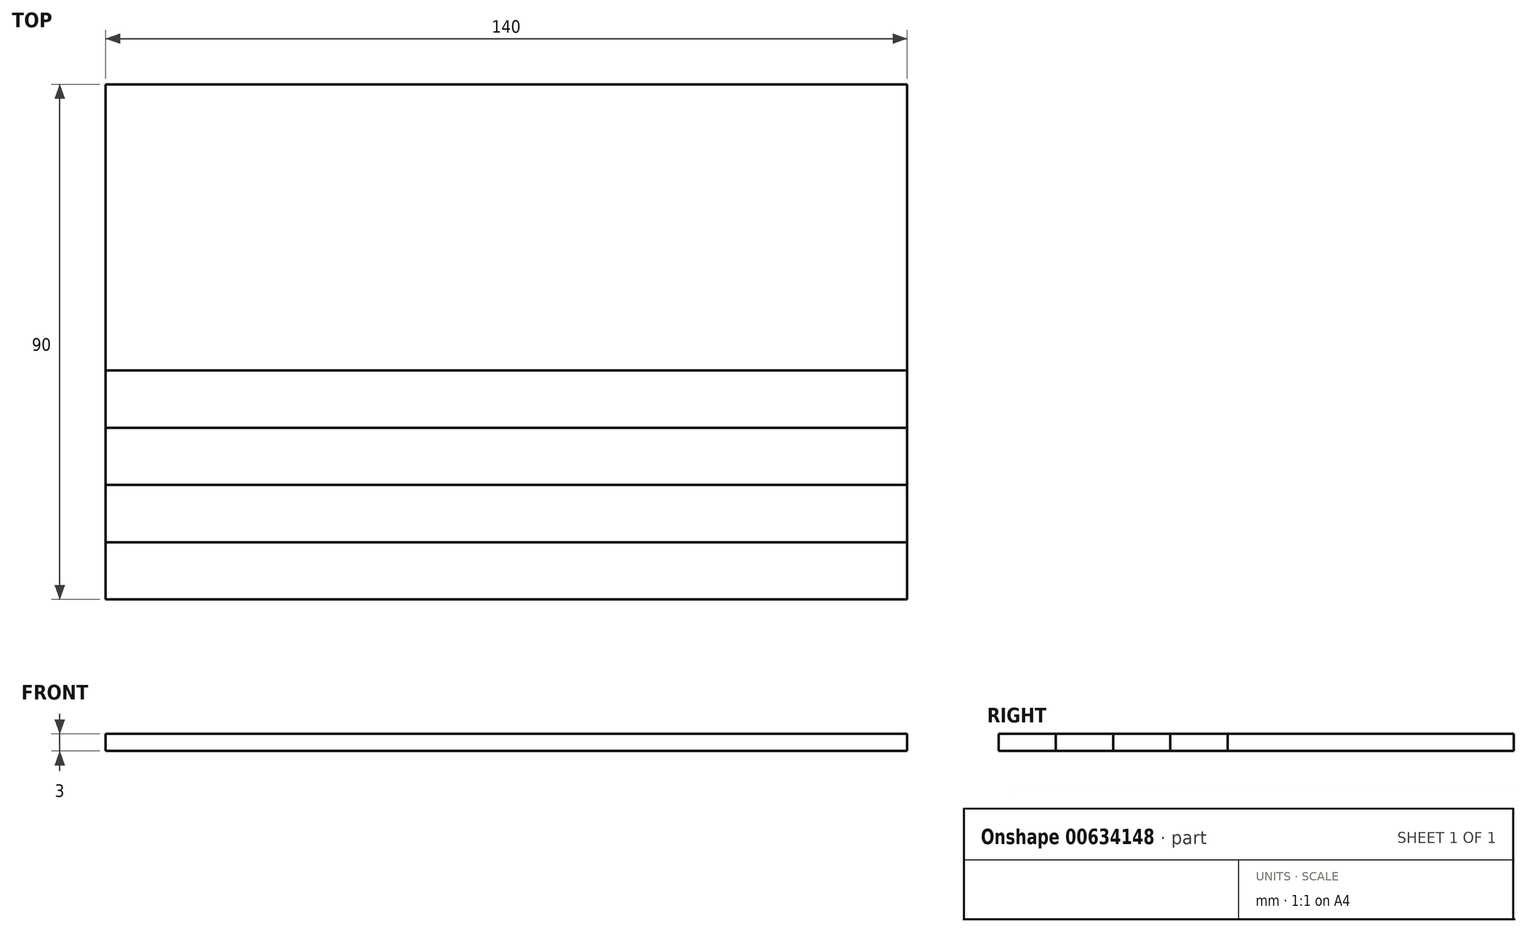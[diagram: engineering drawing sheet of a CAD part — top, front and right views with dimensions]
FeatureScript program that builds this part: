
annotation { "Feature Type Name" : "Feature", "Feature Type Description" : "" }
export const myFeature = defineFeature(function(context is Context, id is Id, definition is map)
    precondition{}
    {
        {
            var Q0;
            Q0=qCreatedBy(makeId("Right.planeOp"),FACE);
            var sketch = newSketch(context, id + "F0", { "sketchPlane" : qUnion([Q0])});
            skLineSegment(sketch, "E0.bottom", {"start": v(-10, 3) * mm, "end": v(0, 3) * mm});
            skLineSegment(sketch, "E0.top", {"start": v(-10, 0) * mm, "end": v(0, 0) * mm});
            skLineSegment(sketch, "E0.left", {"start": v(-10, 3) * mm, "end": v(-10, 0) * mm});
            skLineSegment(sketch, "E0.right", {"start": v(0, 3) * mm, "end": v(0, 0) * mm});
            skLineSegment(sketch, "E1.1.0.0", {"start": v(0, 0) * mm, "end": v(10, 0) * mm});
            skLineSegment(sketch, "E1.1.0.1", {"start": v(0, 3) * mm, "end": v(10, 3) * mm});
            skLineSegment(sketch, "E1.1.0.2", {"start": v(10, 3) * mm, "end": v(10, 0) * mm});
            skLineSegment(sketch, "E1.2.0.0", {"start": v(10, 0) * mm, "end": v(20, 0) * mm});
            skLineSegment(sketch, "E1.2.0.1", {"start": v(10, 3) * mm, "end": v(20, 3) * mm});
            skLineSegment(sketch, "E1.2.0.2", {"start": v(20, 3) * mm, "end": v(20, 0) * mm});
            skLineSegment(sketch, "E1.2.0.3", {"start": v(10, 3) * mm, "end": v(10, 0) * mm});
            skLineSegment(sketch, "E1.3.0.0", {"start": v(20, 0) * mm, "end": v(30, 0) * mm});
            skLineSegment(sketch, "E1.3.0.1", {"start": v(20, 3) * mm, "end": v(30, 3) * mm});
            skLineSegment(sketch, "E1.3.0.2", {"start": v(30, 3) * mm, "end": v(30, 0) * mm});
            skLineSegment(sketch, "E1.3.0.3", {"start": v(20, 3) * mm, "end": v(20, 0) * mm});
            skLineSegment(sketch, "E1.4.0.0", {"start": v(30, 0) * mm, "end": v(40, 0) * mm});
            skLineSegment(sketch, "E1.4.0.1", {"start": v(30, 3) * mm, "end": v(40, 3) * mm});
            skLineSegment(sketch, "E1.4.0.2", {"start": v(40, 3) * mm, "end": v(40, 0) * mm});
            skLineSegment(sketch, "E1.4.0.3", {"start": v(30, 3) * mm, "end": v(30, 0) * mm});
            skLineSegment(sketch, "E1.5.0.0", {"start": v(40, 0) * mm, "end": v(50, 0) * mm});
            skLineSegment(sketch, "E1.5.0.1", {"start": v(40, 3) * mm, "end": v(50, 3) * mm});
            skLineSegment(sketch, "E1.5.0.2", {"start": v(50, 3) * mm, "end": v(50, 0) * mm});
            skLineSegment(sketch, "E1.5.0.3", {"start": v(40, 3) * mm, "end": v(40, 0) * mm});
            skLineSegment(sketch, "E1.6.0.0", {"start": v(50, 0) * mm, "end": v(60, 0) * mm});
            skLineSegment(sketch, "E1.6.0.1", {"start": v(50, 3) * mm, "end": v(60, 3) * mm});
            skLineSegment(sketch, "E1.6.0.2", {"start": v(60, 3) * mm, "end": v(60, 0) * mm});
            skLineSegment(sketch, "E1.6.0.3", {"start": v(50, 3) * mm, "end": v(50, 0) * mm});
            skLineSegment(sketch, "E1.7.0.0", {"start": v(60, 0) * mm, "end": v(70, 0) * mm});
            skLineSegment(sketch, "E1.7.0.1", {"start": v(60, 3) * mm, "end": v(70, 3) * mm});
            skLineSegment(sketch, "E1.7.0.2", {"start": v(70, 3) * mm, "end": v(70, 0) * mm});
            skLineSegment(sketch, "E1.7.0.3", {"start": v(60, 3) * mm, "end": v(60, 0) * mm});
            skLineSegment(sketch, "E1.8.0.0", {"start": v(70, 0) * mm, "end": v(80, 0) * mm});
            skLineSegment(sketch, "E1.8.0.1", {"start": v(70, 3) * mm, "end": v(80, 3) * mm});
            skLineSegment(sketch, "E1.8.0.2", {"start": v(80, 3) * mm, "end": v(80, 0) * mm});
            skLineSegment(sketch, "E1.8.0.3", {"start": v(70, 3) * mm, "end": v(70, 0) * mm});
            skLineSegment(sketch, "E1.direction1", {"start": v(-10, 0) * mm, "end": v(0, 0) * mm, "construction": true});
            skSolve(sketch);
        }
        {
            var Q0;
            Q0=makeQuery(id+"F0.imprint","IMPRINT",FACE,{"disambiguationData":[TD([[makeQuery(id+"F0.imprint","IMPRINT",EDGE,{"derivedFrom":sQuery(id+"F0.wireOp",EDGE,"E0.bottom")}),-1.0]])]});
            var Q1;
            Q1=makeQuery(id+"F0.imprint","IMPRINT",FACE,{"disambiguationData":[TD([[makeQuery(id+"F0.imprint","IMPRINT",EDGE,{"derivedFrom":sQuery(id+"F0.wireOp",EDGE,"E1.2.0.0")}),1.0]])]});
            var Q2;
            Q2=makeQuery(id+"F0.imprint","IMPRINT",FACE,{"disambiguationData":[TD([[makeQuery(id+"F0.imprint","IMPRINT",EDGE,{"derivedFrom":sQuery(id+"F0.wireOp",EDGE,"E1.4.0.0")}),1.0]])]});
            var Q3;
            Q3=makeQuery(id+"F0.imprint","IMPRINT",FACE,{"disambiguationData":[TD([[makeQuery(id+"F0.imprint","IMPRINT",EDGE,{"derivedFrom":sQuery(id+"F0.wireOp",EDGE,"E1.6.0.0")}),1.0]])]});
            var Q4;
            Q4=makeQuery(id+"F0.imprint","IMPRINT",FACE,{"disambiguationData":[TD([[makeQuery(id+"F0.imprint","IMPRINT",EDGE,{"derivedFrom":sQuery(id+"F0.wireOp",EDGE,"E1.8.0.0")}),1.0]])]});
            extrude(context, id + "F1", {"entities" : qUnion([Q0, Q1, Q2, Q3, Q4]), "depth" : 140 * mm, "offsetDistance" : 25 * mm});
        }
        {
            var Q0;
            Q0=makeQuery(id+"F0.imprint","IMPRINT",FACE,{"disambiguationData":[TD([[makeQuery(id+"F0.imprint","IMPRINT",EDGE,{"derivedFrom":sQuery(id+"F0.wireOp",EDGE,"E1.1.0.0")}),1.0]])]});
            var Q1;
            Q1=makeQuery(id+"F0.imprint","IMPRINT",FACE,{"disambiguationData":[TD([[makeQuery(id+"F0.imprint","IMPRINT",EDGE,{"derivedFrom":sQuery(id+"F0.wireOp",EDGE,"E1.3.0.0")}),1.0]])]});
            var Q2;
            Q2=makeQuery(id+"F0.imprint","IMPRINT",FACE,{"disambiguationData":[TD([[makeQuery(id+"F0.imprint","IMPRINT",EDGE,{"derivedFrom":sQuery(id+"F0.wireOp",EDGE,"E1.5.0.0")}),1.0]])]});
            var Q3;
            Q3=makeQuery(id+"F0.imprint","IMPRINT",FACE,{"disambiguationData":[TD([[makeQuery(id+"F0.imprint","IMPRINT",EDGE,{"derivedFrom":sQuery(id+"F0.wireOp",EDGE,"E1.7.0.0")}),1.0]])]});
            extrude(context, id + "F2", {"entities" : qUnion([Q0, Q1, Q2, Q3]), "depth" : 140 * mm, "offsetDistance" : 25 * mm});
        }
        {
            var Q0;
            Q0=makeQuery(id+"F1.opExtrude","SWEPT_FACE",FACE,{"disambiguationData":[OSD([sQuery(id+"F0.wireOp",EDGE,"E1.8.0.1")])]});
            var sketch = newSketch(context, id + "F3", { "sketchPlane" : qUnion([Q0])});
            skLineSegment(sketch, "E2.bottom", {"start": v(0, 80) * mm, "end": v(60, 80) * mm});
            skLineSegment(sketch, "E2.top", {"start": v(0, 40) * mm, "end": v(60, 40) * mm});
            skLineSegment(sketch, "E2.left", {"start": v(0, 80) * mm, "end": v(0, 40) * mm});
            skLineSegment(sketch, "E2.right", {"start": v(60, 80) * mm, "end": v(60, 40) * mm});
            skSolve(sketch);
        }
        {
            var Q0;
            Q0 = qSketchRegion(id + "F3", true);
            var Q1;
            Q1=makeQuery(id+"F1.opExtrude","SWEPT_FACE",FACE,{"disambiguationData":[OSD([sQuery(id+"F0.wireOp",EDGE,"E1.4.0.0")])]});
            extrude(context, id + "F4", {"entities" : qUnion([Q0]), "operationType" : NewBodyOperationType.REMOVE, "endBound" : BoundingType.UP_TO_SURFACE, "oppositeDirection" : true, "depth" : 25 * mm, "endBoundEntityFace" : qUnion([Q1]), "offsetDistance" : 25 * mm});
        }
        {
            var Q0;
            {var subQ0=sQuery(id+"F3.wireOp",EDGE,"E2.top");Q0=makeQuery(id+"F3.imprint","IMPRINT",FACE,{"disambiguationData":[TD([[makeQuery(id+"F3.imprint","IMPRINT",EDGE,{"derivedFrom":subQ0}),1.0]])]});}
            var Q1;
            {var subQ0=sQuery(id+"F3.wireOp",EDGE,"E2.bottom");Q1=makeQuery(id+"F3.imprint","IMPRINT",FACE,{"disambiguationData":[TD([[makeQuery(id+"F3.imprint","IMPRINT",EDGE,{"derivedFrom":subQ0}),1.0]])]});}
            var Q2;
            Q2=makeQuery(id+"F2.opExtrude","SWEPT_FACE",FACE,{"disambiguationData":[OSD([sQuery(id+"F0.wireOp",EDGE,"E1.5.0.0")])]});
            extrude(context, id + "F5", {"entities" : qUnion([Q0, Q1]), "operationType" : NewBodyOperationType.ADD, "endBound" : BoundingType.UP_TO_SURFACE, "oppositeDirection" : true, "depth" : 25 * mm, "endBoundEntityFace" : qUnion([Q2]), "offsetDistance" : 25 * mm});
        }
    });
